# Revit family: xLavatory-Four_Station-Sloan-Designer_Weir_Series-DSWD-84000
name_source: partatom
category: Plumbing Fixtures
revit_build: Autodesk Revit 2014 (Build: 20130308_1515(x64)
units: mm (PartAtom-declared; Revit-internal decimal feet)

## types (1)
- DSWD-84000
    ADA Compliant = Yes
    Assembly Code = D2010300
    Basin Shape = Rectangular
    CW Connection = Yes
    CWFU = 1.5
    Cold Water Connection Diameter = 1/2"
    Cold Water Connection Height = 24"
    Cold Water Connection Radius = 1/4"
    Cold Water Connection Width = 3"
    Default Elevation = 34"
    Description = Four Station Weir Deck Lavatory
    Faucet Hole Punch = 0"
    Faucet Holes = Yes
    Faucet Width = 30"
    Finish = Natural Stone-Sloan-DSC001-Designer White
    HW Connection = Yes
    HWFU = 1.5
    Height = 5"
    Hot Water Connection Diameter = 1/2"
    Hot Water Connection Height = 24"
    Hot Water Connection Width = 3"
    IAPMO Compliance = cUPC
    Installation Type = Wall Mounted
    Length = 22"
    Manufacturer = SLOAN
    Material = Natural Stone-Sloan-DSC001-Designer White
    Model = DSWD-84000
    Price = Prices may vary. Please consult Manufacturer Representative for most up-to-date price list.
    Product Documentation Link = https://www.sloan.com
    Product Page URL = https://www.sloan.com
    Soap Dispenser Hole Punch = 0"
    Soap Dispenser Holes = Yes
    URL = https://www.sloan.com
    Vent Connection = No
    WFU = 2
    Warranty Information = 3 Year Limited Warranty
    Waste Connection = Yes
    Waste Connection Diameter = 1 1/2"
    Waste Connection Height = 20"
    Waste Connection Radius = 3/4"
    Width = 120"

## geometry (parser evidence)
native form markers: Sweep x3
no freeform markers — native parametric forms only
